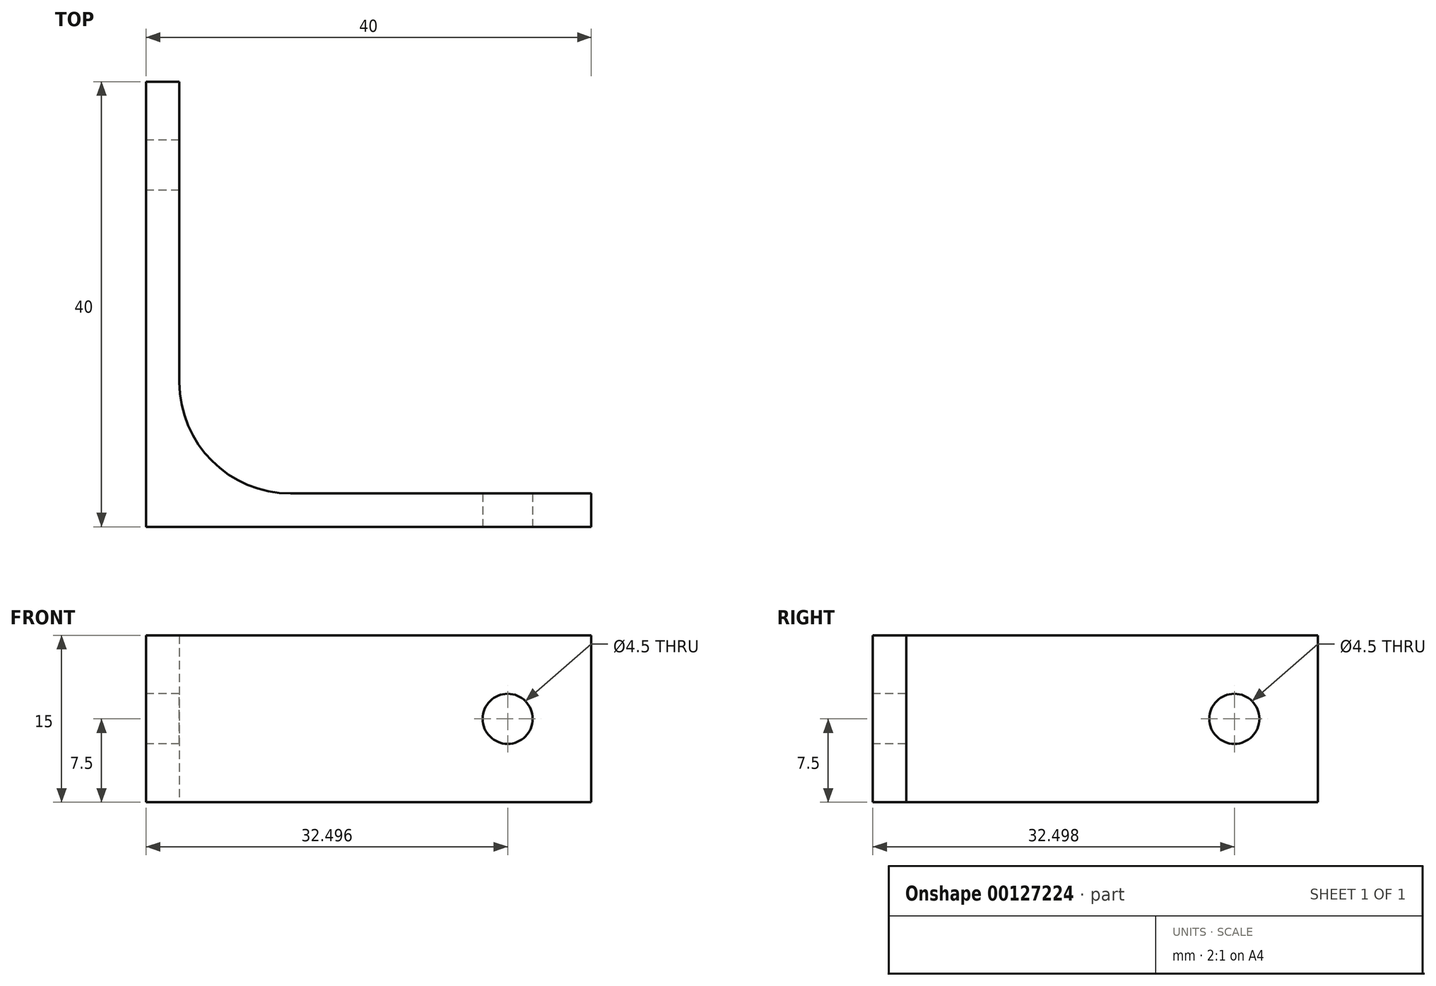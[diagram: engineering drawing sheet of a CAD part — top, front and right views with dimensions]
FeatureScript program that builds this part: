
annotation { "Feature Type Name" : "Feature", "Feature Type Description" : "" }
export const myFeature = defineFeature(function(context is Context, id is Id, definition is map)
    precondition{}
    {
        {
            var Q0;
            Q0=qCreatedBy(makeId("Top.planeOp"),FACE);
            var sketch = newSketch(context, id + "F0", { "sketchPlane" : qUnion([Q0])});
            skLineSegment(sketch, "E0.bottom", {"start": v(-26.23, 31.85) * mm, "end": v(-23.23, 31.85) * mm});
            skLineSegment(sketch, "E0.top", {"start": v(-26.23, -8.15) * mm, "end": v(-23.23, -8.15) * mm});
            skLineSegment(sketch, "E0.left", {"start": v(-26.23, 31.85) * mm, "end": v(-26.23, -8.15) * mm});
            skLineSegment(sketch, "E0.right", {"start": v(-23.23, 31.85) * mm, "end": v(-23.23, -8.15) * mm});
            skLineSegment(sketch, "E1.bottom", {"start": v(-23.23, -8.15) * mm, "end": v(13.77, -8.15) * mm});
            skLineSegment(sketch, "E1.top", {"start": v(-23.23, -5.15) * mm, "end": v(13.77, -5.15) * mm});
            skLineSegment(sketch, "E1.left", {"start": v(-23.23, -8.15) * mm, "end": v(-23.23, -5.15) * mm});
            skLineSegment(sketch, "E1.right", {"start": v(13.77, -8.15) * mm, "end": v(13.77, -5.15) * mm});
            skSolve(sketch);
        }
        {
            var Q0;
            Q0=makeQuery(id+"F0.imprint","IMPRINT",FACE,{"disambiguationData":[TD([[makeQuery(id+"F0.imprint","IMPRINT",EDGE,{"derivedFrom":sQuery(id+"F0.wireOp",EDGE,"E0.bottom")}),-1.0]])]});
            var Q1;
            Q1=makeQuery(id+"F0.imprint","IMPRINT",FACE,{"disambiguationData":[TD([[makeQuery(id+"F0.imprint","IMPRINT",EDGE,{"derivedFrom":sQuery(id+"F0.wireOp",EDGE,"E1.bottom")}),1.0]])]});
            extrude(context, id + "F1", {"entities" : qUnion([Q0, Q1]), "depth" : 15 * mm});
        }
        {
            var Q0;
            Q0=makeQuery(id+"F1.opExtrude","SWEPT_FACE",FACE,{"disambiguationData":[OSD([sQuery(id+"F0.wireOp",EDGE,"E0.top"),sQuery(id+"F0.wireOp",EDGE,"E1.bottom")])]});
            var sketch = newSketch(context, id + "F2", { "sketchPlane" : qUnion([Q0])});
            skPoint(sketch, "E2", {"position": v(6.27, 7.5) * mm});
            skSolve(sketch);
        }
        {
            var Q0;
            Q0=makeQuery(id+"F1.opExtrude","SWEPT_FACE",FACE,{"disambiguationData":[OSD([sQuery(id+"F0.wireOp",EDGE,"E0.left")])]});
            var sketch = newSketch(context, id + "F3", { "sketchPlane" : qUnion([Q0])});
            skSolve(sketch);
        }
        {
            var Q0;
            {var subQ0=sQuery(id+"F0.wireOp",EDGE,"E0.left");Q0=makeQuery(id+"F3.imprint","IMPRINT",FACE,{"disambiguationData":[TD([[makeQuery(id+"F3.imprint","IMPRINT",EDGE,{"derivedFrom":makeQuery(id+"F1.opExtrude","CAP_EDGE",EDGE,{"disambiguationData":[OSD([subQ0])],"isStart":true})}),1.0]])]});}
            var sketch = newSketch(context, id + "F4", { "sketchPlane" : qUnion([Q0])});
            skPoint(sketch, "E3", {"position": v(-24.35, 7.5) * mm});
            skSolve(sketch);
        }
        {
            var Q0;
            Q0=sQuery(id+"F4.wireOp",VERTEX,"E3");
            var Q1;
            Q1=makeQuery(id+"F1.opExtrude","SWEPT_BODY",BODY,{"disambiguationData":[OSD([sQuery(id+"F0.wireOp",EDGE,"E0.bottom"),sQuery(id+"F0.wireOp",EDGE,"E0.top"),sQuery(id+"F0.wireOp",EDGE,"E0.left"),sQuery(id+"F0.wireOp",EDGE,"E0.right"),sQuery(id+"F0.wireOp",EDGE,"E1.bottom"),sQuery(id+"F0.wireOp",EDGE,"E1.top"),sQuery(id+"F0.wireOp",EDGE,"E1.right")])]});
            hole(context, id + "F6", {"style" : HoleStyle.SIMPLE, "endStyle" : HoleEndStyle.THROUGH, "holeDiameter" : 4.5 * mm, "locations" : qUnion([Q0]), "scope" : qUnion([Q1]), "isTappedThrough" : true});
        }
        {
            var Q0;
            Q0=sQuery(id+"F2.wireOp",VERTEX,"E2");
            var Q1;
            Q1=makeQuery(id+"F1.opExtrude","SWEPT_BODY",BODY,{"disambiguationData":[OSD([sQuery(id+"F0.wireOp",EDGE,"E0.bottom"),sQuery(id+"F0.wireOp",EDGE,"E0.top"),sQuery(id+"F0.wireOp",EDGE,"E0.left"),sQuery(id+"F0.wireOp",EDGE,"E0.right"),sQuery(id+"F0.wireOp",EDGE,"E1.bottom"),sQuery(id+"F0.wireOp",EDGE,"E1.top"),sQuery(id+"F0.wireOp",EDGE,"E1.right")])]});
            hole(context, id + "F7", {"style" : HoleStyle.SIMPLE, "endStyle" : HoleEndStyle.THROUGH, "holeDiameter" : 4.5 * mm, "locations" : qUnion([Q0]), "scope" : qUnion([Q1]), "isTappedThrough" : true});
        }
        {
            var Q0;
            Q0=makeQuery(id+"F1.opExtrude","SWEPT_EDGE",EDGE,{"disambiguationData":[OSD([sQuery(id+"F0.wireOp",EDGE,"E0.right"),sQuery(id+"F0.wireOp",EDGE,"E1.top"),sQuery(id+"F0.wireOp",EDGE,"E1.left")])]});
            fillet(context, id + "F5", {"entities" : qUnion([Q0]), "radius" : 10 * mm, "tangentPropagation" : true, "allowEdgeOverflow" : false});
        }
    });
